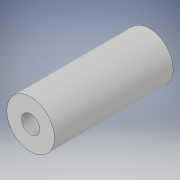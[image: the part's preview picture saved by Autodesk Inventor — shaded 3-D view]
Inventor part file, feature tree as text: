
AUTODESK INVENTOR PART (.ipt)
format: ipt  version: 2018 (Build 220112000, 112)  size: 94,720 bytes
history: native  units: in
note: dims shown in document units (in); Inventor stores cm internally (conversion verified against a paired STEP export)
features: extrude x1, sketch x1
ambient origin geometry x8: Origin, YZ Plane, XZ Plane, XY Plane, X Axis, Y Axis, Z Axis, Center Point
bodies: Solid1 (feature_tree)
feature tree (2):
  extrude  "Extrusion1"  Depth=1.248in
  sketch  "Sketch1"  dims[d0=0.19in d1=0.5in d2=1.248in d3=0.0in]
